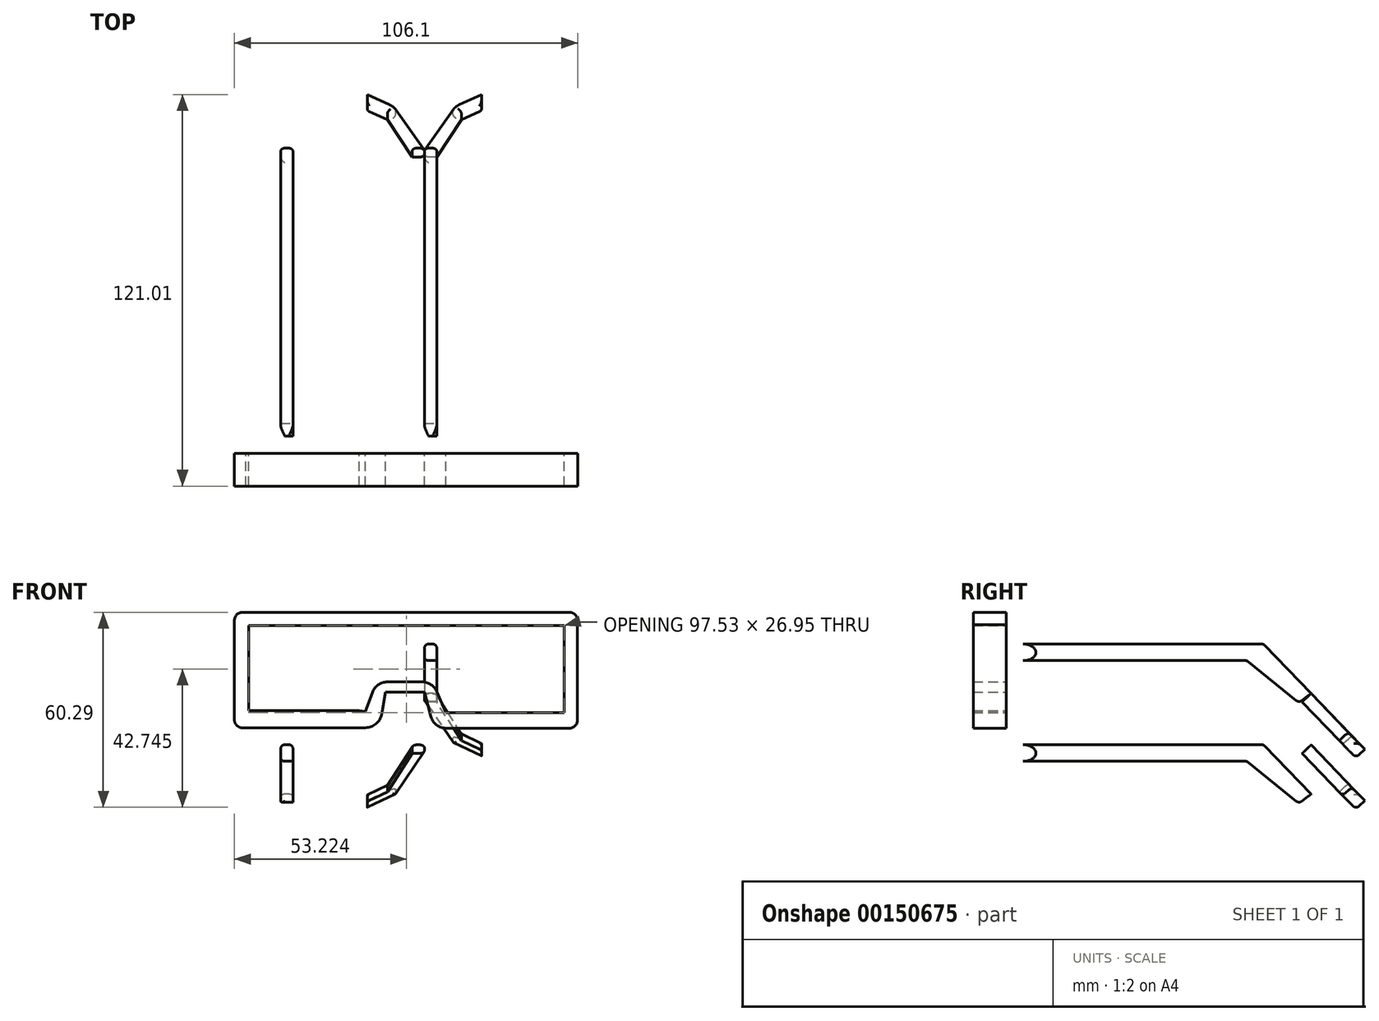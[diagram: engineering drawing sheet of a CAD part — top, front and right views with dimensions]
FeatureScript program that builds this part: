
annotation { "Feature Type Name" : "Feature", "Feature Type Description" : "" }
export const myFeature = defineFeature(function(context is Context, id is Id, definition is map)
    precondition{}
    {
        {
            var Q0;
            Q0=qCreatedBy(makeId("Front.planeOp"),FACE);
            var sketch = newSketch(context, id + "F0", { "sketchPlane" : qUnion([Q0])});
            skLineSegment(sketch, "E0", {"start": v(-56.62, 34.22) * mm, "end": v(44.98, 34.22) * mm});
            skLineSegment(sketch, "E1", {"start": v(47.3, 30.34) * mm, "end": v(47.3, -1.65) * mm});
            skLineSegment(sketch, "E2", {"start": v(47.3, -1.65) * mm, "end": v(2.9, -1.65) * mm});
            skLineSegment(sketch, "E3", {"start": v(2.9, -1.65) * mm, "end": v(0, 9.6) * mm});
            skLineSegment(sketch, "E4", {"start": v(0, 9.6) * mm, "end": v(-12.02, 9.6) * mm});
            skLineSegment(sketch, "E5", {"start": v(-54.3, 30.15) * mm, "end": v(43.24, 30.15) * mm});
            skLineSegment(sketch, "E6", {"start": v(43.24, 30.15) * mm, "end": v(43.24, 3.2) * mm});
            skLineSegment(sketch, "E7", {"start": v(43.24, 3.2) * mm, "end": v(6.6, 3.2) * mm});
            skLineSegment(sketch, "E8", {"start": v(6.6, 3.2) * mm, "end": v(2.52, 12.7) * mm});
            skLineSegment(sketch, "E9", {"start": v(2.52, 12.7) * mm, "end": v(-14.93, 12.7) * mm});
            skLineSegment(sketch, "E10", {"start": v(-12.02, 9.6) * mm, "end": v(-13.96, -1.45) * mm});
            skLineSegment(sketch, "E11", {"start": v(-13.96, -1.45) * mm, "end": v(-55.26, -1.45) * mm});
            skLineSegment(sketch, "E12", {"start": v(-58.75, 30.93) * mm, "end": v(-58.75, -1.65) * mm});
            skLineSegment(sketch, "E13", {"start": v(-58.75, -1.65) * mm, "end": v(-55.26, -1.45) * mm});
            skLineSegment(sketch, "E14", {"start": v(-54.3, 30.15) * mm, "end": v(-54.3, 3.78) * mm});
            skLineSegment(sketch, "E15", {"start": v(-54.3, 3.78) * mm, "end": v(-20.15, 3.78) * mm});
            skLineSegment(sketch, "E16", {"start": v(-14.93, 12.7) * mm, "end": v(-18.21, 3.59) * mm});
            skLineSegment(sketch, "E17", {"start": v(-18.21, 3.59) * mm, "end": v(-20.15, 3.78) * mm});
            skLineSegment(sketch, "E18", {"start": v(-58.75, 30.93) * mm, "end": v(-58.75, 34.22) * mm});
            skLineSegment(sketch, "E19", {"start": v(-58.75, 34.22) * mm, "end": v(-56.62, 34.22) * mm});
            skLineSegment(sketch, "E20", {"start": v(44.98, 34.22) * mm, "end": v(47.44, 34.22) * mm});
            skLineSegment(sketch, "E21", {"start": v(47.44, 34.22) * mm, "end": v(47.3, 30.34) * mm});
            skSolve(sketch);
        }
        {
            var Q0;
            Q0 = qSketchRegion(id + "F0", true);
            extrude(context, id + "F1", {"entities" : qUnion([Q0]), "depth" : 10.16 * mm});
        }
        {
            var Q0;
            Q0=makeQuery(id+"F1.opExtrude","SWEPT_EDGE",EDGE,{"disambiguationData":[OSD([sQuery(id+"F0.wireOp",EDGE,"E12"),sQuery(id+"F0.wireOp",EDGE,"E13")])]});
            var Q1;
            Q1=makeQuery(id+"F1.opExtrude","SWEPT_EDGE",EDGE,{"disambiguationData":[OSD([sQuery(id+"F0.wireOp",EDGE,"E1"),sQuery(id+"F0.wireOp",EDGE,"E2")])]});
            var Q2;
            Q2=makeQuery(id+"F1.opExtrude","SWEPT_EDGE",EDGE,{"disambiguationData":[OSD([sQuery(id+"F0.wireOp",EDGE,"E18"),sQuery(id+"F0.wireOp",EDGE,"E19")])]});
            var Q3;
            Q3=makeQuery(id+"F1.opExtrude","SWEPT_EDGE",EDGE,{"disambiguationData":[OSD([sQuery(id+"F0.wireOp",EDGE,"E20"),sQuery(id+"F0.wireOp",EDGE,"E21")])]});
            fillet(context, id + "F2", {"entities" : qUnion([Q0, Q1, Q2, Q3]), "radius" : 2.54 * mm, "tangentPropagation" : true, "allowEdgeOverflow" : false});
        }
        {
            var Q0;
            Q0=makeQuery(id+"F1.opExtrude","SWEPT_EDGE",EDGE,{"disambiguationData":[OSD([sQuery(id+"F0.wireOp",EDGE,"E10"),sQuery(id+"F0.wireOp",EDGE,"E11")])]});
            var Q1;
            Q1=makeQuery(id+"F1.opExtrude","SWEPT_EDGE",EDGE,{"disambiguationData":[OSD([sQuery(id+"F0.wireOp",EDGE,"E2"),sQuery(id+"F0.wireOp",EDGE,"E3")])]});
            fillet(context, id + "F3", {"entities" : qUnion([Q0, Q1]), "radius" : 5.08 * mm, "tangentPropagation" : true, "allowEdgeOverflow" : false});
        }
        {
            var Q0;
            Q0=makeQuery(id+"F1.opExtrude","SWEPT_EDGE",EDGE,{"disambiguationData":[OSD([sQuery(id+"F0.wireOp",EDGE,"E9"),sQuery(id+"F0.wireOp",EDGE,"E16")])]});
            var Q1;
            Q1=makeQuery(id+"F1.opExtrude","SWEPT_EDGE",EDGE,{"disambiguationData":[OSD([sQuery(id+"F0.wireOp",EDGE,"E8"),sQuery(id+"F0.wireOp",EDGE,"E9")])]});
            fillet(context, id + "F4", {"entities" : qUnion([Q0, Q1]), "radius" : 5.08 * mm, "tangentPropagation" : true, "allowEdgeOverflow" : false});
        }
        {
            var Q0;
            Q0=qCreatedBy(makeId("Right.planeOp"),FACE);
            var sketch = newSketch(context, id + "F5", { "sketchPlane" : qUnion([Q0])});
            skEllipse(sketch, "E22", {"center": v(5.29, 21.82) * mm, "majorRadius": 3.92 * mm, "minorRadius": 2.56 * mm, "majorAxis": v(1, 0)});
            skLineSegment(sketch, "E23", {"start": v(5.29, 24.38) * mm, "end": v(79.6, 24.38) * mm});
            skLineSegment(sketch, "E24", {"start": v(5.29, 19.26) * mm, "end": v(74.5, 19.26) * mm});
            skLineSegment(sketch, "E25", {"start": v(74.5, 19.26) * mm, "end": v(90.5, 6.3) * mm});
            skLineSegment(sketch, "E26", {"start": v(90.5, 6.3) * mm, "end": v(94.28, 9.1) * mm});
            skLineSegment(sketch, "E27", {"start": v(79.6, 24.38) * mm, "end": v(94.28, 9.1) * mm});
            skSolve(sketch);
        }
        {
            var Q0;
            {var subQ1=sQuery(id+"F5.wireOp",EDGE,"E23");Q0=makeQuery(id+"F5.imprint","IMPRINT",FACE,{"disambiguationData":[TD([[makeQuery(id+"F5.imprint","IMPRINT",EDGE,{"derivedFrom":subQ1}),-1.0]])]});}
            extrude(context, id + "F6", {"entities" : qUnion([Q0]), "depth" : 3.8 * mm});
        }
        {
            var Q0;
            Q0=sQuery(id+"F5.wireOp",EDGE,"E22");
            extrude(context, id + "F7", {"bodyType" : ToolBodyType.SURFACE, "surfaceEntities" : qUnion([Q0]), "depth" : 3.8 * mm});
        }
        {
            var Q0;
            Q0=makeQuery(id+"F6.opExtrude","SWEPT_FACE",FACE,{"disambiguationData":[OSD([sQuery(id+"F5.wireOp",EDGE,"E27")])]});
            var sketch = newSketch(context, id + "F8", { "sketchPlane" : qUnion([Q0])});
            skLineSegment(sketch, "E28", {"start": v(0, -58.78) * mm, "end": v(-8.8, -76.86) * mm});
            skLineSegment(sketch, "E29", {"start": v(-8.8, -76.86) * mm, "end": v(-17.63, -82.7) * mm});
            skLineSegment(sketch, "E30", {"start": v(-17.63, -82.7) * mm, "end": v(-17.63, -79.43) * mm});
            skLineSegment(sketch, "E31", {"start": v(-17.63, -79.43) * mm, "end": v(-11.46, -75.36) * mm});
            skLineSegment(sketch, "E32", {"start": v(-11.46, -75.36) * mm, "end": v(-3.8, -58.78) * mm});
            skLineSegment(sketch, "E33", {"start": v(-3.8, -58.78) * mm, "end": v(0, -58.78) * mm});
            skSolve(sketch);
        }
        {
            var Q0;
            Q0 = qSketchRegion(id + "F8", true);
            extrude(context, id + "F9", {"entities" : qUnion([Q0]), "operationType" : NewBodyOperationType.ADD, "oppositeDirection" : true, "depth" : 3.8 * mm});
        }
        {
            var Q0;
            Q0=makeQuery(id+"F6.opExtrude","CAP_EDGE",EDGE,{"disambiguationData":[OSD([sQuery(id+"F5.wireOp",EDGE,"E23")])],"isStart":false});
            var Q1;
            Q1=makeQuery(id+"F6.opExtrude","SWEPT_EDGE",EDGE,{"disambiguationData":[OSD([sQuery(id+"F5.wireOp",EDGE,"E23"),sQuery(id+"F5.wireOp",EDGE,"E27")])]});
            var Q2;
            Q2=makeQuery(id+"F6.opExtrude","CAP_EDGE",EDGE,{"disambiguationData":[OSD([sQuery(id+"F5.wireOp",EDGE,"E23")])],"isStart":true});
            var Q3;
            Q3=makeQuery(id+"F6.opExtrude","CAP_EDGE",EDGE,{"disambiguationData":[OSD([sQuery(id+"F5.wireOp",EDGE,"E24")])],"isStart":true});
            var Q4;
            Q4=makeQuery(id+"F6.opExtrude","CAP_EDGE",EDGE,{"disambiguationData":[OSD([sQuery(id+"F5.wireOp",EDGE,"E25")])],"isStart":true});
            var Q5;
            Q5=makeQuery(id+"F6.opExtrude","CAP_EDGE",EDGE,{"disambiguationData":[OSD([sQuery(id+"F5.wireOp",EDGE,"E27")])],"isStart":true});
            var Q6;
            Q6=makeQuery(id+"F6.opExtrude","CAP_EDGE",EDGE,{"disambiguationData":[OSD([sQuery(id+"F5.wireOp",EDGE,"E27")])],"isStart":false});
            var Q7;
            Q7=makeQuery(id+"F6.opExtrude","SWEPT_EDGE",EDGE,{"disambiguationData":[OSD([sQuery(id+"F5.wireOp",EDGE,"E24"),sQuery(id+"F5.wireOp",EDGE,"E25")])]});
            var Q8;
            Q8=makeQuery(id+"F6.opExtrude","SWEPT_EDGE",EDGE,{"disambiguationData":[OSD([sQuery(id+"F5.wireOp",EDGE,"E25"),sQuery(id+"F5.wireOp",EDGE,"E26")])]});
            fillet(context, id + "F10", {"entities" : qUnion([Q0, Q1, Q2, Q3, Q4, Q5, Q6, Q7, Q8]), "radius" : 1.27 * mm, "tangentPropagation" : true, "allowEdgeOverflow" : false});
        }
        {
            var Q0;
            Q0=makeQuery(id+"F9.opExtrude","CAP_EDGE",EDGE,{"disambiguationData":[OSD([sQuery(id+"F8.wireOp",EDGE,"E28")])],"isStart":false});
            var Q1;
            Q1=makeQuery(id+"F9.opExtrude","CAP_EDGE",EDGE,{"disambiguationData":[OSD([sQuery(id+"F8.wireOp",EDGE,"E28")])],"isStart":true});
            var Q2;
            Q2=makeQuery(id+"F9.opExtrude","CAP_EDGE",EDGE,{"disambiguationData":[OSD([sQuery(id+"F8.wireOp",EDGE,"E29")])],"isStart":false});
            var Q3;
            Q3=makeQuery(id+"F9.opExtrude","CAP_EDGE",EDGE,{"disambiguationData":[OSD([sQuery(id+"F8.wireOp",EDGE,"E32")])],"isStart":true});
            var Q4;
            Q4=makeQuery(id+"F9.opExtrude","CAP_EDGE",EDGE,{"disambiguationData":[OSD([sQuery(id+"F8.wireOp",EDGE,"E31")])],"isStart":true});
            var Q5;
            Q5=makeQuery(id+"F9.opExtrude","SWEPT_EDGE",EDGE,{"disambiguationData":[OSD([sQuery(id+"F8.wireOp",EDGE,"E30"),sQuery(id+"F8.wireOp",EDGE,"E31")])]});
            fillet(context, id + "F11", {"entities" : qUnion([Q0, Q1, Q2, Q3, Q4, Q5]), "radius" : 1.27 * mm, "tangentPropagation" : true, "allowEdgeOverflow" : false});
        }
        {
            var Q0;
            Q0=makeQuery(id+"F9.opExtrude","SWEPT_BODY",BODY,{"disambiguationData":[OSD([sQuery(id+"F8.wireOp",EDGE,"E28"),sQuery(id+"F8.wireOp",EDGE,"E29"),sQuery(id+"F8.wireOp",EDGE,"E30"),sQuery(id+"F8.wireOp",EDGE,"E31"),sQuery(id+"F8.wireOp",EDGE,"E32"),sQuery(id+"F8.wireOp",EDGE,"E33")])]});
            transform(context, id + "F12", {"entities" : qUnion([Q0]), "transformType" : TransformType.TRANSLATION_3D, "dx" : 0 * mm, "dy" : 0 * mm, "dz" : -15.88 * mm, "makeCopy" : true});
        }
        {
            var Q0;
            Q0=makeQuery(id+"F12.opPattern","COPY",BODY,{"derivedFrom":makeQuery(id+"F9.opExtrude","SWEPT_BODY",BODY,{"disambiguationData":[OSD([sQuery(id+"F8.wireOp",EDGE,"E28"),sQuery(id+"F8.wireOp",EDGE,"E29"),sQuery(id+"F8.wireOp",EDGE,"E30"),sQuery(id+"F8.wireOp",EDGE,"E31"),sQuery(id+"F8.wireOp",EDGE,"E32"),sQuery(id+"F8.wireOp",EDGE,"E33")])]}),"instanceName":"1"});
            var Q1;
            Q1=qCreatedBy(makeId("Right.planeOp"),FACE);
            mirror(context, id + "F13", {"entities" : qUnion([Q0]), "mirrorPlane" : qUnion([Q1])});
        }
        {
            var Q0;
            Q0=makeQuery(id+"F12.opPattern","COPY",BODY,{"derivedFrom":makeQuery(id+"F9.opExtrude","SWEPT_BODY",BODY,{"disambiguationData":[OSD([sQuery(id+"F8.wireOp",EDGE,"E28"),sQuery(id+"F8.wireOp",EDGE,"E29"),sQuery(id+"F8.wireOp",EDGE,"E30"),sQuery(id+"F8.wireOp",EDGE,"E31"),sQuery(id+"F8.wireOp",EDGE,"E32"),sQuery(id+"F8.wireOp",EDGE,"E33")])]}),"instanceName":"1"});
            deleteBodies(context, id + "F14", {"entities" : qUnion([Q0])});
        }
        {
            var Q0;
            Q0=makeQuery(id+"F6.opExtrude","SWEPT_BODY",BODY,{"disambiguationData":[OSD([sQuery(id+"F5.wireOp",EDGE,"E22"),sQuery(id+"F5.wireOp",EDGE,"E23"),sQuery(id+"F5.wireOp",EDGE,"E24"),sQuery(id+"F5.wireOp",EDGE,"E25"),sQuery(id+"F5.wireOp",EDGE,"E26"),sQuery(id+"F5.wireOp",EDGE,"E27")])]});
            transform(context, id + "F15", {"entities" : qUnion([Q0]), "transformType" : TransformType.TRANSLATION_3D, "dx" : -44.45 * mm, "dy" : 0 * mm, "dz" : -31.1 * mm, "makeCopy" : true});
        }
    });
